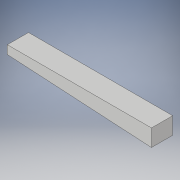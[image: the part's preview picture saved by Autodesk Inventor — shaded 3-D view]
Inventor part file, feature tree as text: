
AUTODESK INVENTOR PART (.ipt)
format: ipt  version: 2017 (Build 210142000, 142)  size: 93,696 bytes
history: native  units: in
note: dims shown in document units (in); Inventor stores cm internally (conversion verified against a paired STEP export)
features: sketch x1, extrude x1
ambient origin geometry x8: Origin, YZ Plane, XZ Plane, XY Plane, X Axis, Y Axis, Z Axis, Center Point
bodies: Solid1 (feature_tree)
feature tree (2):
  sketch  "Sketch1"  dims[d0=17.0in d1=2.0in d2=2.5in d3=0.0in d4=1.0in d5=2.0in]
  extrude  "Extrusion1"  Depth=2.0in
